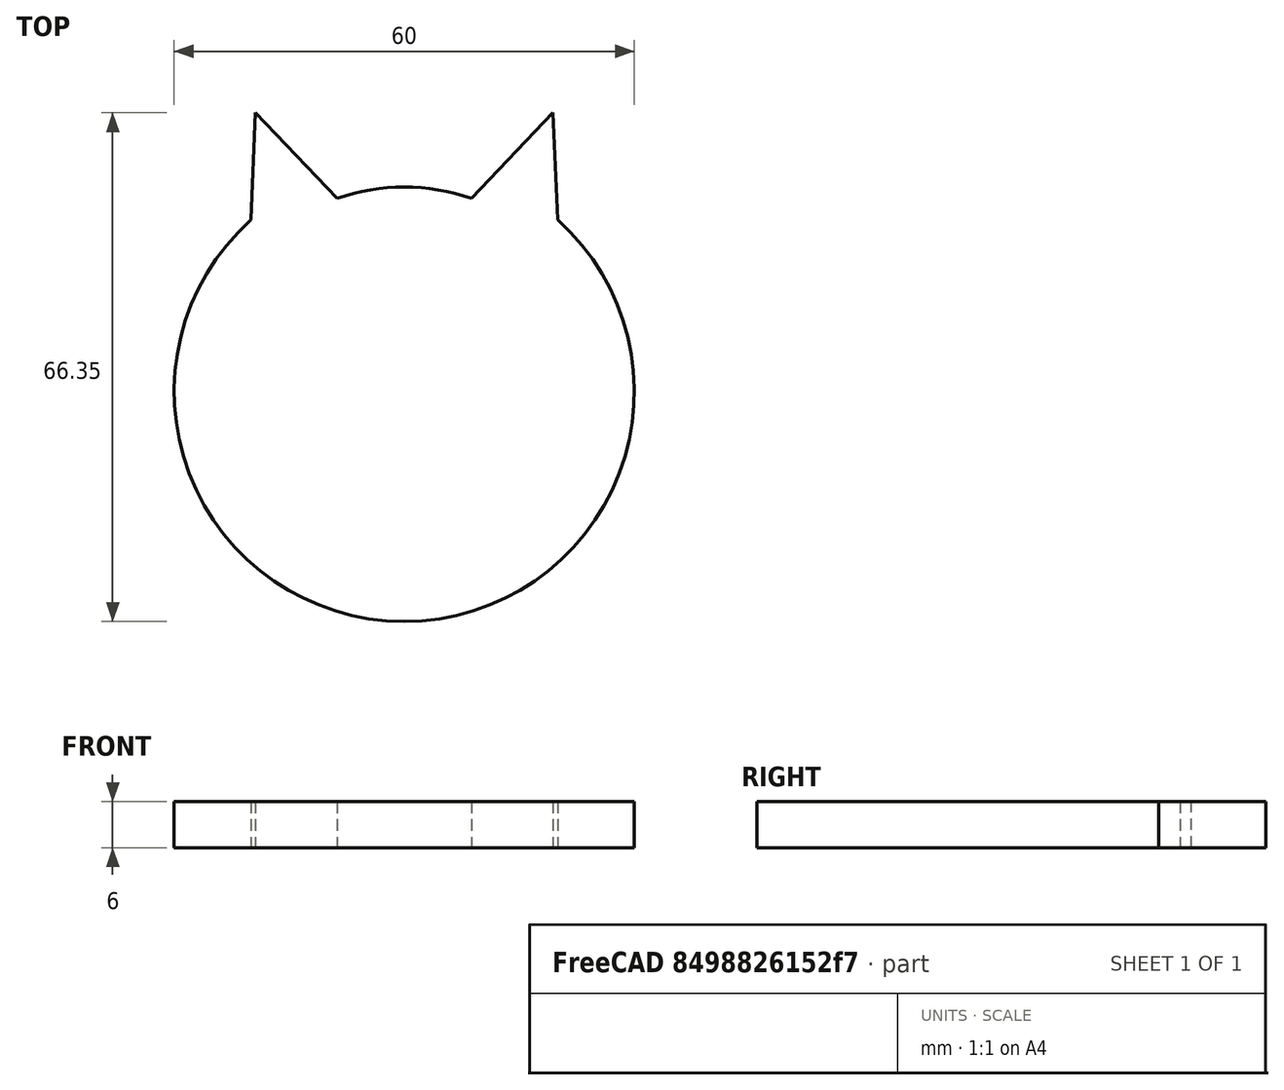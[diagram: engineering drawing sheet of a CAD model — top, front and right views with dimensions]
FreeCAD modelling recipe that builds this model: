
FCSTD DOCUMENT  (FreeCAD 0.20R29177 +233 (Git))
Label: gato?
License: Creative Commons Attribution-ShareAlike
LicenseURL: http://creativecommons.org/licenses/by-sa/4.0/
objects: Sketcher::SketchObject×2, PartDesign::Body×2, PartDesign::Pad×1
note: 6 computed .brp shape members not serialized (recipe doc carries the construction recipe); baked Part::Feature solids carry a one-line shape summary decoded from their .brp

FEATURE [Sketcher::SketchObject] Sketch
  FullyConstrained = false
  MapMode = 5
  Support = -> [XY_Plane]
  sketch-geometry (6):
    g0: ArcOfCircle CenterX=-1.1e-15 CenterY=0 CenterZ=0 NormalX=0 NormalY=0 NormalZ=1 AngleXU=0 Radius=30 StartAngle=2.30052 EndAngle=7.12425
    g1: LineSegment StartX=-20 StartY=22.3607 StartZ=0 EndX=-19.4003 EndY=36.3478 EndZ=0
    g2: LineSegment StartX=-19.4003 StartY=36.3478 StartZ=0 EndX=-8.74978 EndY=25.1823 EndZ=0
    g3: LineSegment StartX=20 StartY=22.3607 StartZ=0 EndX=19.4003 EndY=36.3478 EndZ=0
    g4: LineSegment StartX=19.4003 StartY=36.3478 StartZ=0 EndX=8.74978 EndY=25.1823 EndZ=0
    g5: ArcOfCircle CenterX=-1.1e-15 CenterY=0 CenterZ=0 NormalX=0 NormalY=0 NormalZ=1 AngleXU=0 Radius=26.6591 StartAngle=1.23639 EndAngle=1.9052
  constraints (14):
    c: Symmetric(g0,g0,g-2)
    c: DistanceX(g0) = -20
    c: Coincident(g0,g-1)
    c: Radius(g0) = 30
    c: Coincident(g1,g0)
    c: Coincident(g2,g1)
    c: Coincident(g3,g0)
    c: Coincident(g4,g3)
    c: Symmetric(g1,g3,g-2)
    c: Symmetric(g2,g4,g-2)
    c: Distance(g1) = 14
    c: Coincident(g5,g0)
    c: Coincident(g5,g2)
    c: Coincident(g5,g4)
FEATURE [PartDesign::Pad] Pad
  Direction = (0,0,1)
  Length = 6
  Length2 = 10
  Profile = -> Sketch
  ReferenceAxis = -> Sketch [N_Axis]
  Refine = true
  Reversed = true
  Type = 0
FEATURE [PartDesign::Body] Body
  Group = -> [Sketch,Pad]
  Origin = -> Origin
  Tip = -> Pad
FEATURE [Sketcher::SketchObject] Sketch001
  FullyConstrained = false
  MapMode = 5
  Support = -> [XY_Plane001]
  sketch-geometry (81):
    g0: LineSegment StartX=0 StartY=-2.88675 StartZ=0 EndX=2.5 EndY=1.44338 EndZ=0
    g1: LineSegment StartX=2.5 StartY=1.44338 StartZ=0 EndX=-2.5 EndY=1.44338 EndZ=0
    g2: LineSegment StartX=-2.5 StartY=1.44338 StartZ=0 EndX=0 EndY=-2.88675 EndZ=0
    g3: Circle CenterX=0 CenterY=0 CenterZ=0 NormalX=0 NormalY=0 NormalZ=1 AngleXU=0 Radius=2.88675
    g4-g40: Circle x37 (B-spline internal-alignment scaffolding for g41; pole/knot coordinates omitted)
    g41: BSplineCurve PolesCount=37 KnotsCount=35 Degree=3 IsPeriodic=0
    g42-g76: GeomPoint x35 (B-spline internal-alignment scaffolding for g41; pole/knot coordinates omitted)
    g77: Circle CenterX=-12 CenterY=14 CenterZ=0 NormalX=0 NormalY=0 NormalZ=1 AngleXU=0 Radius=4
    g78: Circle CenterX=12 CenterY=14 CenterZ=0 NormalX=0 NormalY=0 NormalZ=1 AngleXU=0 Radius=4
    g79: Circle CenterX=-10.6121 CenterY=12.56 CenterZ=0 NormalX=0 NormalY=0 NormalZ=1 AngleXU=0 Radius=2
    g80: Circle CenterX=13.3879 CenterY=12.56 CenterZ=0 NormalX=0 NormalY=0 NormalZ=1 AngleXU=0 Radius=2
  constraints (53):
    c: Coincident(g0,g1)
    c: Coincident(g1,g2)
    c: Coincident(g2,g0)
    c: Equal(g0,g1)
    c: Equal(g0,g2)
    c: PointOnObject(g0,g3)
    c: PointOnObject(g1,g3)
    c: PointOnObject(g2,g3)
    c: Coincident(g3,g-1)
    c: PointOnObject(g2,g-2)
    c: DistanceX(g1,g1) = 5
    c: Weight(g4) = 1
    c: PointOnObject(g41,g-2)
    c: Equal(g4, g6-g12) x7
    c: PointOnObject(g12,g11)
    c: Equal(g4,g13)
    c: Equal(g4,g14)
    c: Equal(g4,g15)
    c: PointOnObject(g15,g14)
    c: Equal(g4,g16)
    c: PointOnObject(g16,g15)
    c: Equal(g4,g17)
    c: Equal(g4,g18)
    c: Equal(g4,g19)
    c: PointOnObject(g19,g18)
    c: Equal(g4,g20)
    c: Equal(g4,g21)
    c: Equal(g4,g22)
    c: PointOnObject(g22,g-2)
    c: Equal(g4,g23)
    c: Equal(g4,g24)
    c: PointOnObject(g24,g23)
    c: Equal(g4, g25-g29) x5
    c: Equal(g4, g32-g37) x6
    c: PointOnObject(g37,g36)
    c: Equal(g4,g38)
    c: Equal(g4,g39)
    c: PointOnObject(g39,g38)
    c: Equal(g4,g40)
    c: Coincident(g41,g4)
    c: InternalAlignment(g4-g40 -> g41) x37
    c: InternalAlignment(g42-g76 -> g41) x35
    c: Symmetric(g77,g78,g-2)
    c: Radius(g77) = 4
    c: Radius(g78) = 4
    c: DistanceX(g77,g-1) = 12
    c: DistanceY(g-1,g77) = 14
    c: PointOnObject(g77,g79)
    c: Radius(g79) = 2
    c: PointOnObject(g78,g80)
    c: Radius(g80) = 2
    c: DistanceY(g80) = 12.56
    c: DistanceY(g79) = 12.56
FEATURE [PartDesign::Body] Body001
  Group = -> [Sketch001]
  Origin = -> Origin001
